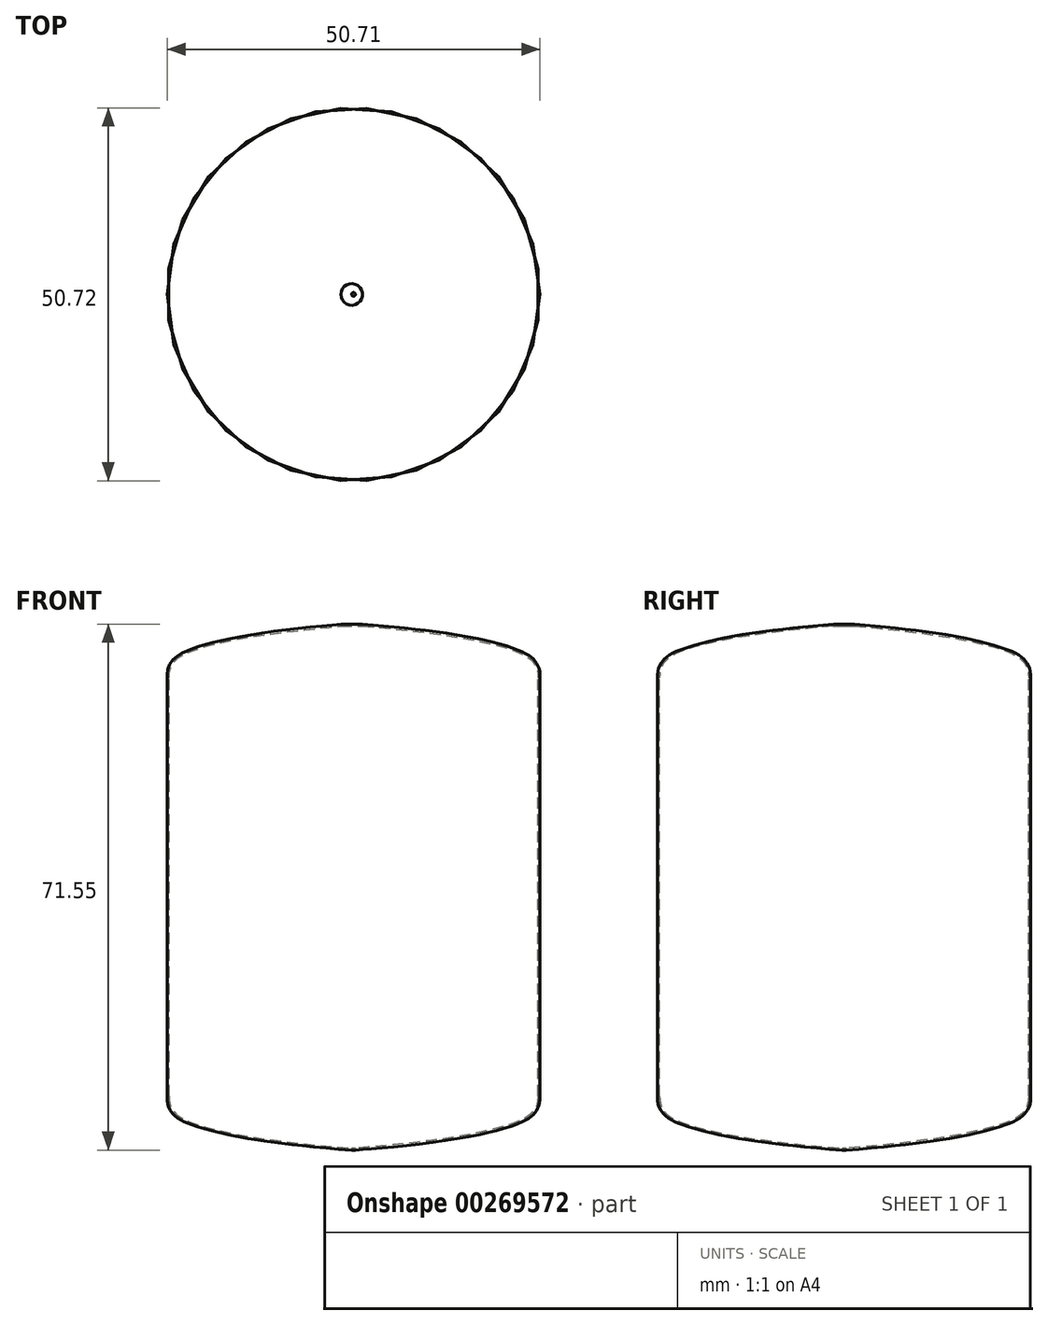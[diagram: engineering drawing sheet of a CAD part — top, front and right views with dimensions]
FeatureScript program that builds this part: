
annotation { "Feature Type Name" : "Feature", "Feature Type Description" : "" }
export const myFeature = defineFeature(function(context is Context, id is Id, definition is map)
    precondition{}
    {
        {
            var Q0;
            Q0=qCreatedBy(makeId("Front.planeOp"),FACE);
            var sketch = newSketch(context, id + "F0", { "sketchPlane" : qUnion([Q0])});
            skLineSegment(sketch, "E0.left", {"start": v(-24.85, 33.24) * mm, "end": v(-24.85, -23.66) * mm});
            skFitSpline(sketch, "E1", {"points": [v(-24.85, 33.24) * mm, v(-22.13, 36.72) * mm, v(0, 40.36) * mm], "startDerivative": vector(0.08, 18.04) * mm, "endDerivative": vector(39.95, 3.15) * mm});
            skLineSegment(sketch, "E2.0", {"start": v(-25.1, 33.24) * mm, "end": v(-25.1, -23.66) * mm});
            skFitSpline(sketch, "E3.0", {"points": [v(-25.1, 33.24) * mm, v(-25.1, 33.63) * mm, v(-25.02, 34.35) * mm, v(-24.65, 35.23) * mm, v(-24.04, 35.94) * mm, v(-23.21, 36.5) * mm, v(-22.17, 37) * mm, v(-20.91, 37.45) * mm, v(-19.45, 37.88) * mm, v(-17.24, 38.42) * mm, v(-14.06, 39.02) * mm, v(-9.72, 39.65) * mm, v(-5, 40.18) * mm, v(-1.69, 40.48) * mm, v(-0.02, 40.6) * mm]});
            skLineSegment(sketch, "E4", {"start": v(-0.02, 40.6) * mm, "end": v(0, 40.36) * mm});
            skLineSegment(sketch, "E5.MirrorCS", {"start": v(-0.02, -31.02) * mm, "end": v(0, -30.77) * mm});
            skFitSpline(sketch, "E6.MirrorCS", {"points": [v(-24.85, -23.66) * mm, v(-22.13, -27.13) * mm, v(0, -30.77) * mm], "startDerivative": vector(0.08, -18.04) * mm, "endDerivative": vector(39.95, -3.15) * mm});
            skFitSpline(sketch, "E7.0", {"points": [v(-25.1, -23.66) * mm, v(-25.1, -24.05) * mm, v(-25.02, -24.76) * mm, v(-24.65, -25.64) * mm, v(-24.04, -26.36) * mm, v(-23.21, -26.93) * mm, v(-22.17, -27.41) * mm, v(-20.91, -27.87) * mm, v(-19.45, -28.3) * mm, v(-17.24, -28.83) * mm, v(-14.06, -29.44) * mm, v(-9.72, -30.07) * mm, v(-5, -30.6) * mm, v(-1.69, -30.9) * mm, v(-0.02, -31.02) * mm]});
            skLineSegment(sketch, "E8", {"start": v(-0.02, -31.02) * mm, "end": v(0, -31.02) * mm});
            skLineSegment(sketch, "E9", {"start": v(0, -31.02) * mm, "end": v(0, -30.77) * mm});
            skLineSegment(sketch, "E10", {"start": v(-25.1, -23.66) * mm, "end": v(-25.1, -23.66) * mm});
            skLineSegment(sketch, "E11", {"start": v(-25.1, 33.24) * mm, "end": v(-25.1, 33.24) * mm});
            skLineSegment(sketch, "E12", {"start": v(-0.02, 40.6) * mm, "end": v(0, 40.6) * mm});
            skLineSegment(sketch, "E13", {"start": v(0, 40.6) * mm, "end": v(0, 40.36) * mm});
            skLineSegment(sketch, "E14", {"start": v(0, 40.36) * mm, "end": v(0, -30.18) * mm});
            skLineSegment(sketch, "E15.0", {"start": v(0.25, 40.36) * mm, "end": v(0.25, -30.18) * mm});
            skSolve(sketch);
        }
        {
            var Q0;
            Q0=makeQuery(id+"F0.imprint","IMPRINT",FACE,{"disambiguationData":[TD([[makeQuery(id+"F0.imprint","IMPRINT",EDGE,{"derivedFrom":sQuery(id+"F0.wireOp",EDGE,"E0.left")}),-1.0]])]});
            var Q1;
            Q1=sQuery(id+"F0.wireOp",EDGE,"E15.0");
            revolve(context, id + "F1", {"entities" : qUnion([Q0]), "axis" : qUnion([Q1]), "revolveType" : RevolveType.FULL});
        }
        {
            var Q0;
            Q0=qCreatedBy(makeId("Front.planeOp"),FACE);
            var sketch = newSketch(context, id + "F2", { "sketchPlane" : qUnion([Q0])});
            skLineSegment(sketch, "E16.bottom", {"start": v(0, 47.16) * mm, "end": v(1.47, 47.16) * mm});
            skLineSegment(sketch, "E16.top", {"start": v(0, -14.3) * mm, "end": v(1.47, -14.3) * mm});
            skLineSegment(sketch, "E16.left", {"start": v(0, 47.16) * mm, "end": v(0, -14.3) * mm});
            skLineSegment(sketch, "E16.right", {"start": v(1.47, 47.16) * mm, "end": v(1.47, -14.3) * mm});
            skSolve(sketch);
        }
        {
            var Q0;
            Q0 = qSketchRegion(id + "F2", true);
            var Q1;
            Q1=sQuery(id+"F2.wireOp",EDGE,"E16.left");
            revolve(context, id + "F3", {"operationType" : NewBodyOperationType.REMOVE, "entities" : qUnion([Q0]), "axis" : qUnion([Q1]), "revolveType" : RevolveType.FULL});
        }
    });
